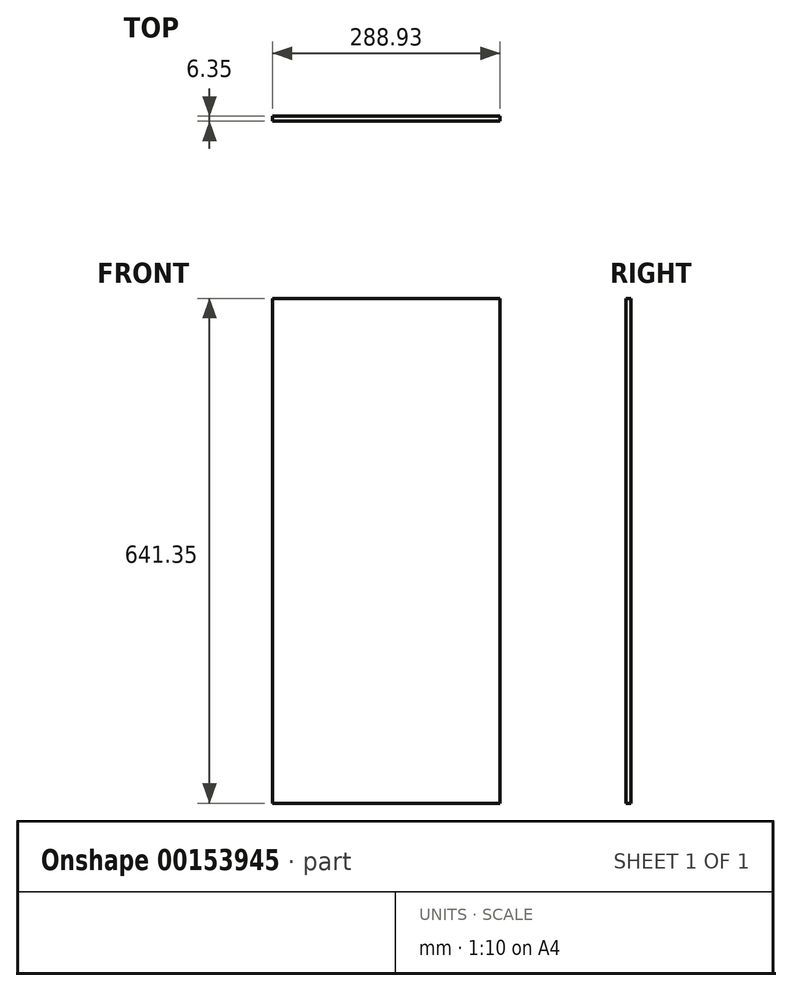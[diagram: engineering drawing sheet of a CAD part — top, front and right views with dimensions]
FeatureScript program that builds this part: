
annotation { "Feature Type Name" : "Feature", "Feature Type Description" : "" }
export const myFeature = defineFeature(function(context is Context, id is Id, definition is map)
    precondition{}
    {
        {
            var Q0;
            Q0=qCreatedBy(makeId("Front.planeOp"),FACE);
            var sketch = newSketch(context, id + "F0", { "sketchPlane" : qUnion([Q0])});
            skLineSegment(sketch, "E0.bottom", {"start": v(0, 0) * mm, "end": v(288.93, 0) * mm});
            skLineSegment(sketch, "E0.top", {"start": v(0, 641.35) * mm, "end": v(288.92, 641.35) * mm});
            skLineSegment(sketch, "E0.left", {"start": v(0, 0) * mm, "end": v(0, 641.35) * mm});
            skLineSegment(sketch, "E0.right", {"start": v(288.93, 0) * mm, "end": v(288.92, 641.35) * mm});
            skSolve(sketch);
        }
        {
            var Q0;
            Q0=makeQuery(id+"F0.imprint","IMPRINT",FACE,{"disambiguationData":[TD([[makeQuery(id+"F0.imprint","IMPRINT",EDGE,{"derivedFrom":sQuery(id+"F0.wireOp",EDGE,"E0.bottom")}),1.0]])]});
            extrude(context, id + "F1", {"entities" : qUnion([Q0]), "depth" : 6.35 * mm});
        }
    });
